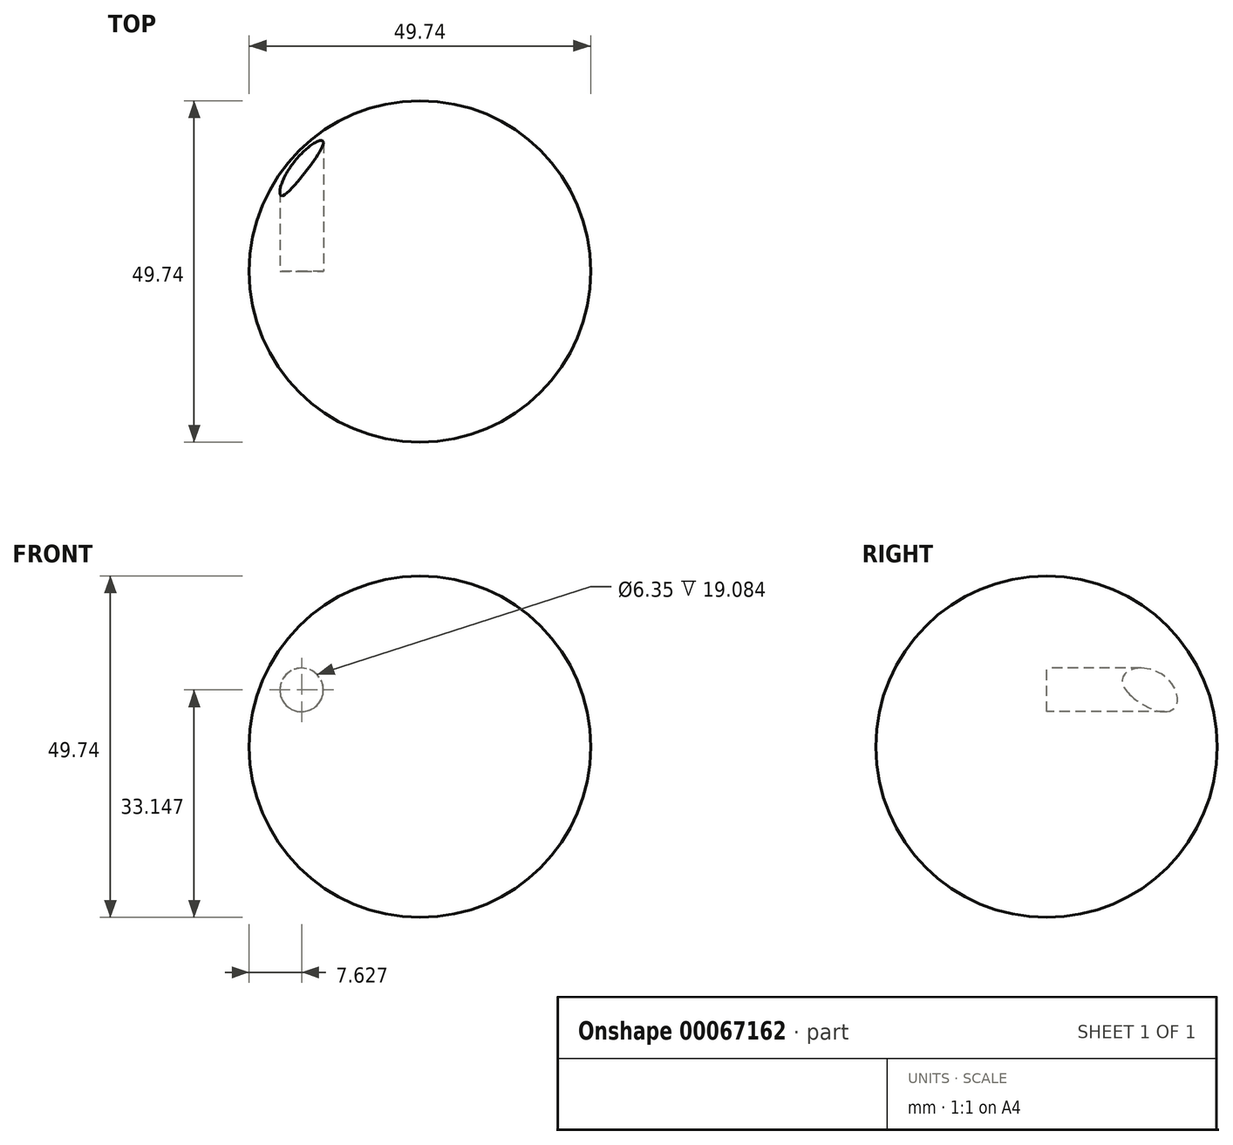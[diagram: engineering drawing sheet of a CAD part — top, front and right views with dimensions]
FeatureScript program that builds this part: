
annotation { "Feature Type Name" : "Feature", "Feature Type Description" : "" }
export const myFeature = defineFeature(function(context is Context, id is Id, definition is map)
    precondition{}
    {
        {
            var Q0;
            Q0=qCreatedBy(makeId("Front.planeOp"),FACE);
            var sketch = newSketch(context, id + "F0", { "sketchPlane" : qUnion([Q0])});
            skCircle(sketch, "E0", {"center": v(0, 0) * mm, "radius": 24.87 * mm});
            skLineSegment(sketch, "E1", {"start": v(0, 44.14) * mm, "end": v(0, -61.85) * mm});
            skSolve(sketch);
        }
        {
            var Q0;
            {var subQ0=sQuery(id+"F0.wireOp",EDGE,"E1");var subQ1=sQuery(id+"F0.wireOp",EDGE,"E0");var subQ2=makeQuery(id+"F0.imprint","INTERSECT",VERTEX,{"disambiguationData":[OD(0.0)],"derivedFrom":[subQ1,subQ0]});Q0=makeQuery(id+"F0.imprint","IMPRINT",FACE,{"disambiguationData":[TD([[makeQuery(id+"F0.imprint","IMPRINT",EDGE,{"disambiguationData":[TD([[subQ2,1.0]])],"derivedFrom":subQ1}),1.0]])]});}
            var Q1;
            Q1=sQuery(id+"F0.wireOp",EDGE,"E1");
            revolve(context, id + "F1", {"entities" : qUnion([Q0]), "axis" : qUnion([Q1]), "revolveType" : RevolveType.FULL});
        }
        {
            var Q0;
            Q0=qCreatedBy(makeId("Front.planeOp"),FACE);
            var sketch = newSketch(context, id + "F2", { "sketchPlane" : qUnion([Q0])});
            skCircle(sketch, "E2", {"center": v(-17.24, 8.28) * mm, "radius": 3.32 * mm});
            skSolve(sketch);
        }
        {
            var Q0;
            Q0=sQuery(id+"F2.wireOp",VERTEX,"E2.center");
            var Q1;
            Q1=makeQuery(id+"F1.opRevolve","SWEPT_BODY",BODY,{"disambiguationData":[OSD([sQuery(id+"F0.wireOp",EDGE,"E0"),sQuery(id+"F0.wireOp",EDGE,"E1")])]});
            hole(context, id + "F3", {"style" : HoleStyle.SIMPLE, "holeDiameter" : 6.35 * mm, "endStyle" : HoleEndStyle.THROUGH, "locations" : qUnion([Q0]), "scope" : qUnion([Q1])});
        }
    });
